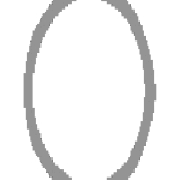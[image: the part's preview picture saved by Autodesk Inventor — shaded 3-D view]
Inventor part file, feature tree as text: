
AUTODESK INVENTOR PART (.ipt)
format: ipt  version: 2021 (Build 250183000, 183)  size: 113,152 bytes
history: native  units: in
note: dims shown in document units (in); Inventor stores cm internally (conversion verified against a paired STEP export)
features: other x4, sketch x3, plane x1
ambient origin geometry x8: Origin, YZ Plane, XZ Plane, XY Plane, X Axis, Y Axis, Z Axis, Center Point
bodies: Solid1 (feature_tree), Body (feature_tree)
feature tree (8):
  other  "Driven Length"
  other  "Frame Generator"
  other  "Start Plane"
  other  "End Plane"
  sketch  "Sketch"  dims[d2=13.0in d4=-0.0in d5=13.0in d6=0.12in d7=0.0in d8=90.0deg d9=13.0in]
  sketch  "Sketch2"  dims[d0=1.0in]
  plane  "Work Plane3"
  sketch  "Sketch3"  dims[d1=0.065in]
